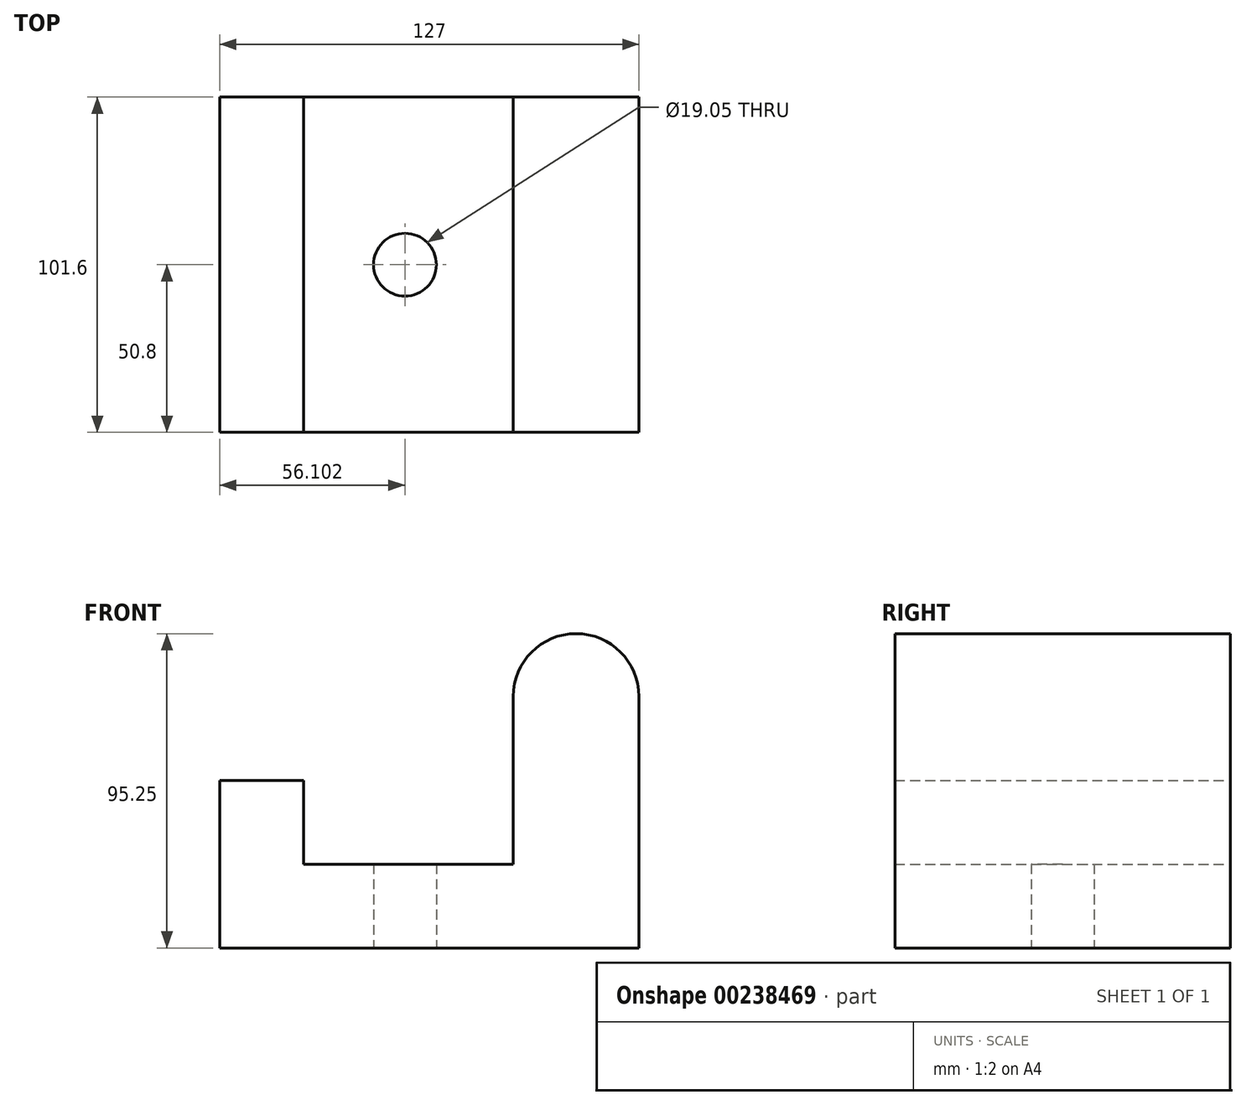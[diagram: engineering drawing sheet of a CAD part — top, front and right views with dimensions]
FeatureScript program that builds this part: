
annotation { "Feature Type Name" : "Feature", "Feature Type Description" : "" }
export const myFeature = defineFeature(function(context is Context, id is Id, definition is map)
    precondition{}
    {
        {
            var Q0;
            Q0=qCreatedBy(makeId("Front.planeOp"),FACE);
            var sketch = newSketch(context, id + "F0", { "sketchPlane" : qUnion([Q0])});
            skLineSegment(sketch, "E0", {"start": v(0, 76.2) * mm, "end": v(0, 0) * mm});
            skLineSegment(sketch, "E1", {"start": v(0, 0) * mm, "end": v(-127, 0) * mm});
            skLineSegment(sketch, "E2", {"start": v(-127, 0) * mm, "end": v(-127, 50.8) * mm});
            skLineSegment(sketch, "E3", {"start": v(-127, 50.8) * mm, "end": v(-101.6, 50.8) * mm});
            skLineSegment(sketch, "E4", {"start": v(-101.6, 50.8) * mm, "end": v(-101.6, 25.4) * mm});
            skLineSegment(sketch, "E5", {"start": v(-101.6, 25.4) * mm, "end": v(-38.1, 25.4) * mm});
            skLineSegment(sketch, "E6", {"start": v(-38.1, 25.4) * mm, "end": v(-38.1, 76.2) * mm});
            skArc(sketch, "E7", {"start": v(-38.1, 76.2) * mm, "mid": v(-19.05, 95.25) * mm, "end": v(0, 76.2) * mm});
            skSolve(sketch);
        }
        {
            var Q0;
            Q0=makeQuery(id+"F0.imprint","IMPRINT",FACE,{"disambiguationData":[TD([[makeQuery(id+"F0.imprint","IMPRINT",EDGE,{"derivedFrom":sQuery(id+"F0.wireOp",EDGE,"E0")}),-1.0]])]});
            extrude(context, id + "F1", {"entities" : qUnion([Q0]), "depth" : 101.6 * mm, "symmetric" : true});
        }
        {
            var Q0;
            Q0=qCreatedBy(makeId("Top.planeOp"),FACE);
            var sketch = newSketch(context, id + "F2", { "sketchPlane" : qUnion([Q0])});
            skLineSegment(sketch, "E8", {"start": v(-70.9, 49.95) * mm, "end": v(-70.9, -49.54) * mm});
            skLineSegment(sketch, "E9", {"start": v(-101.37, 0) * mm, "end": v(-38.15, 0) * mm});
            skPoint(sketch, "E10", {"position": v(-70.9, 0) * mm});
            skPoint(sketch, "E11", {"position": v(-120.44, 75.66) * mm});
            skSolve(sketch);
        }
        {
            var Q0;
            Q0=sQuery(id+"F2.wireOp",VERTEX,"E10");
            var Q1;
            Q1=makeQuery(id+"F1.opExtrude","SWEPT_BODY",BODY,{"disambiguationData":[OSD([sQuery(id+"F0.wireOp",EDGE,"E0"),sQuery(id+"F0.wireOp",EDGE,"E1"),sQuery(id+"F0.wireOp",EDGE,"E2"),sQuery(id+"F0.wireOp",EDGE,"E3"),sQuery(id+"F0.wireOp",EDGE,"E4"),sQuery(id+"F0.wireOp",EDGE,"E5"),sQuery(id+"F0.wireOp",EDGE,"E6"),sQuery(id+"F0.wireOp",EDGE,"E7")])]});
            hole(context, id + "F3", {"style" : HoleStyle.SIMPLE, "endStyle" : HoleEndStyle.THROUGH, "oppositeDirection" : true, "holeDiameter" : 19.05 * mm, "tappedDepth" : 12.7 * mm, "tapClearance" : 3, "locations" : qUnion([Q0]), "scope" : qUnion([Q1])});
        }
    });
